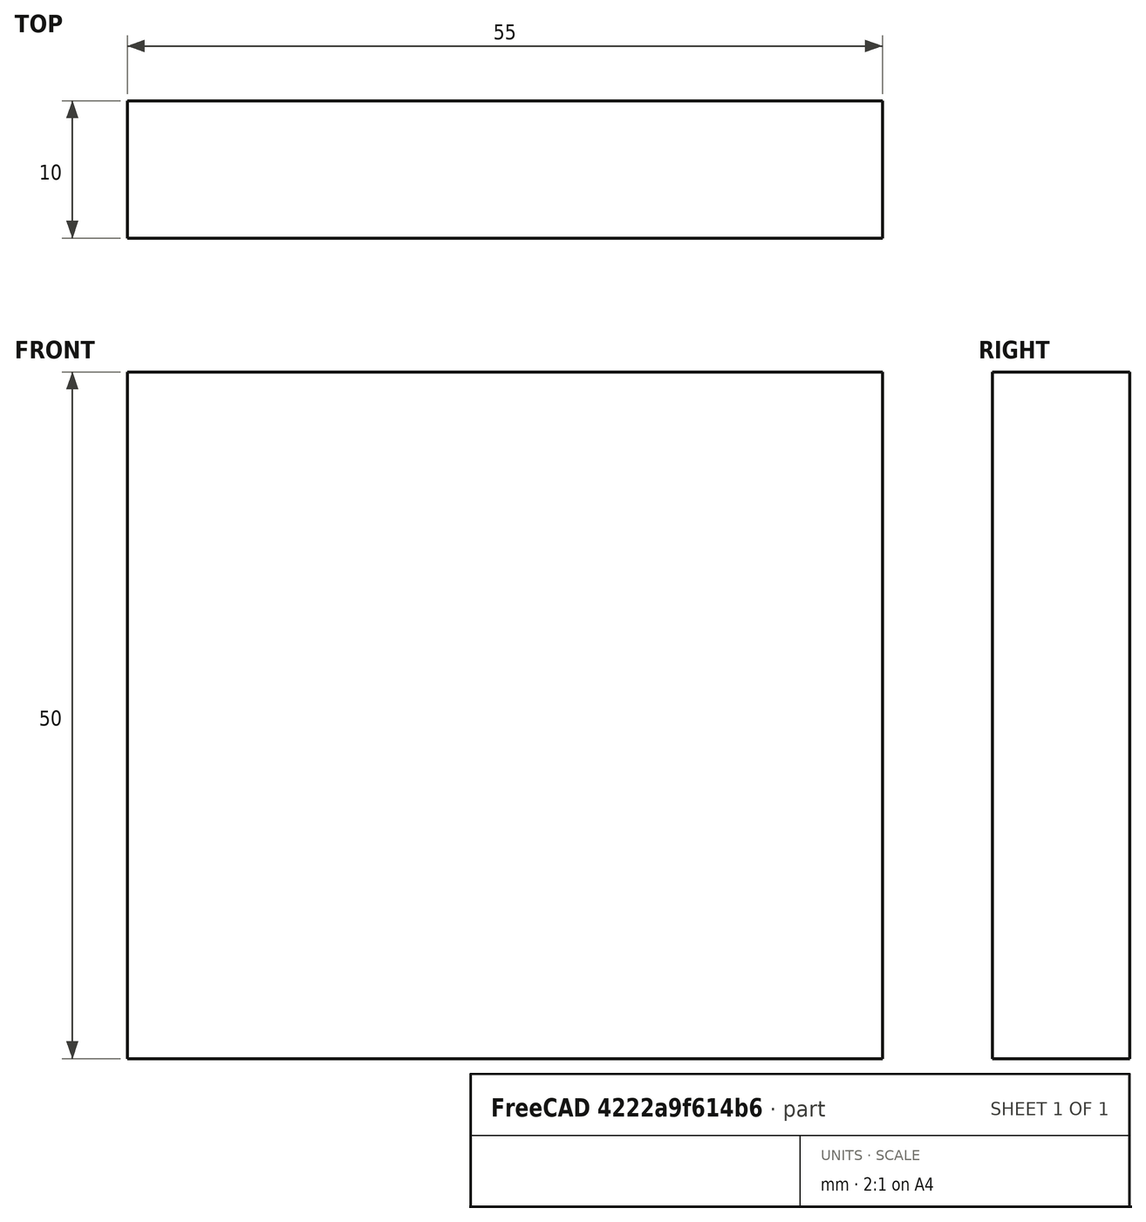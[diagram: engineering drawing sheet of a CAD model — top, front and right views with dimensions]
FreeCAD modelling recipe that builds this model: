
FCSTD DOCUMENT  (FreeCAD 0.15R4671 (Git))
Label: Flat Bar 55x10 EN10058 S235JR
License: All rights reserved
LicenseURL: http://en.wikipedia.org/wiki/All_rights_reserved
objects: Sketcher::SketchObject×1, Part::Extrusion×1
note: 2 computed .brp shape members not serialized (recipe doc carries the construction recipe); baked Part::Feature solids carry a one-line shape summary decoded from their .brp

FEATURE [Sketcher::SketchObject] Sketch
  sketch-geometry (4):
    g0: LineSegment StartX=-27.5 StartY=-5 StartZ=0 EndX=27.5 EndY=-5 EndZ=0
    g1: LineSegment StartX=27.5 StartY=-5 StartZ=0 EndX=27.5 EndY=5 EndZ=0
    g2: LineSegment StartX=27.5 StartY=5 StartZ=0 EndX=-27.5 EndY=5 EndZ=0
    g3: LineSegment StartX=-27.5 StartY=5 StartZ=0 EndX=-27.5 EndY=-5 EndZ=0
  constraints (12):
    c: Coincident(g0,g1)
    c: Coincident(g1,g2)
    c: Coincident(g2,g3)
    c: Coincident(g3,g0)
    c: Horizontal(g0)
    c: Horizontal(g2)
    c: Vertical(g1)
    c: Vertical(g3)
    c: Symmetric(g1,g2,g-2)
    c: Symmetric(g0,g1,g-1)
    c: DistanceY(g1) = 10
    c: DistanceX(g0) = 55
FEATURE [Part::Extrusion] Extrude  label="Flat Bar 55x10 EN10058 S235JR"
  Base = -> Sketch
  Dir = (0,0,50)
  Solid = true
